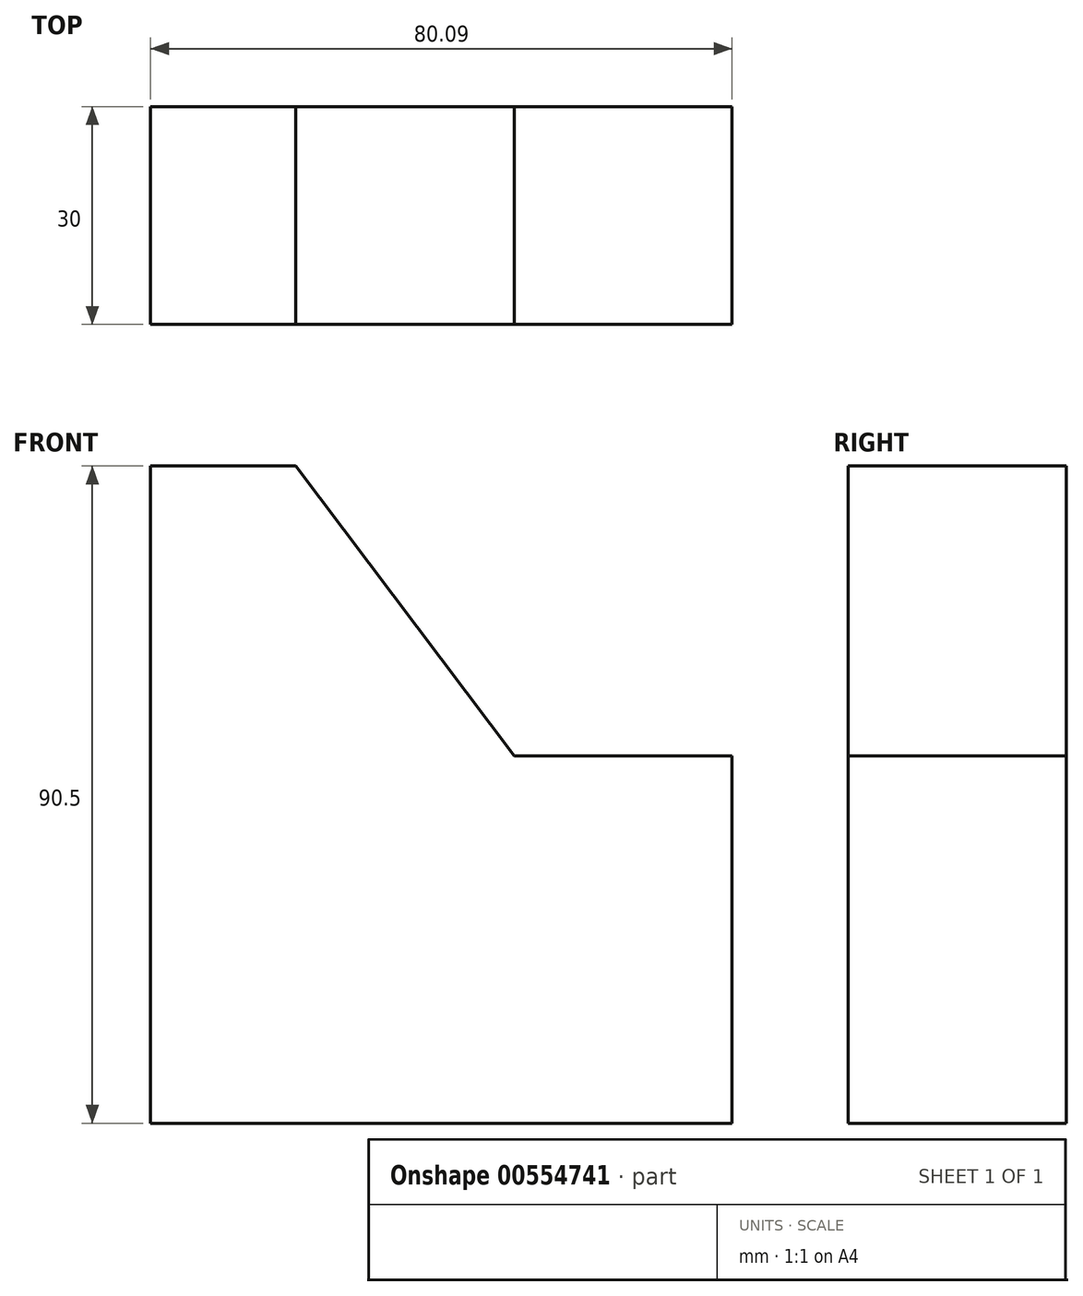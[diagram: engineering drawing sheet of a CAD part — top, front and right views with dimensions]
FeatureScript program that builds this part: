
annotation { "Feature Type Name" : "Feature", "Feature Type Description" : "" }
export const myFeature = defineFeature(function(context is Context, id is Id, definition is map)
    precondition{}
    {
        {
            var Q0;
            Q0=qCreatedBy(makeId("Front.planeOp"),FACE);
            var sketch = newSketch(context, id + "F0", { "sketchPlane" : qUnion([Q0])});
            skLineSegment(sketch, "E0", {"start": v(-93.6, 58.53) * mm, "end": v(-73.6, 58.53) * mm});
            skLineSegment(sketch, "E1", {"start": v(-73.6, 58.53) * mm, "end": v(-43.5, 18.6) * mm});
            skLineSegment(sketch, "E2", {"start": v(-43.5, 18.6) * mm, "end": v(-13.5, 18.6) * mm});
            skLineSegment(sketch, "E3", {"start": v(-13.5, 18.6) * mm, "end": v(-13.5, -31.97) * mm});
            skLineSegment(sketch, "E4", {"start": v(-13.5, -31.97) * mm, "end": v(-93.6, -31.97) * mm});
            skLineSegment(sketch, "E5", {"start": v(-93.6, -31.97) * mm, "end": v(-93.6, 58.53) * mm});
            skSolve(sketch);
        }
        {
            var Q0;
            Q0 = qSketchRegion(id + "F0", true);
            extrude(context, id + "F1", {"entities" : qUnion([Q0]), "depth" : 30 * mm, "offsetDistance" : 25 * mm});
        }
    });
